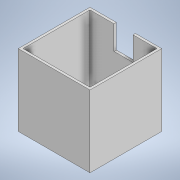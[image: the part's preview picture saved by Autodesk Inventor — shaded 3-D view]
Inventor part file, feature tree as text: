
AUTODESK INVENTOR PART (.ipt)
format: ipt  version: 2022 (Build 260153000, 153)  size: 116,736 bytes
history: native  units: mm
features: extrude x3, sketch x3
ambient origin geometry x8: Origin, YZ Plane, XZ Plane, XY Plane, X Axis, Y Axis, Z Axis, Center Point
bodies: Solid1 (feature_tree)
feature tree (6):
  extrude  "Extrusion1"  Depth=150.0mm
  extrude  "Extrusion2"  Depth=5.0mm
  extrude  "Extrusion3"  Depth=5.0mm
  sketch  "Sketch1"  dims[d0=150.0mm d1=150.0mm]
  sketch  "Sketch2"  dims[d2=150.0mm d3=0.0mm d4=5.0mm]
  sketch  "Sketch3"  dims[d5=5.0mm d6=5.0mm d7=5.0mm d8=145.0mm d9=0.0mm d10=20.0mm d11=20.0mm d12=50.0mm d13=0.0mm]
